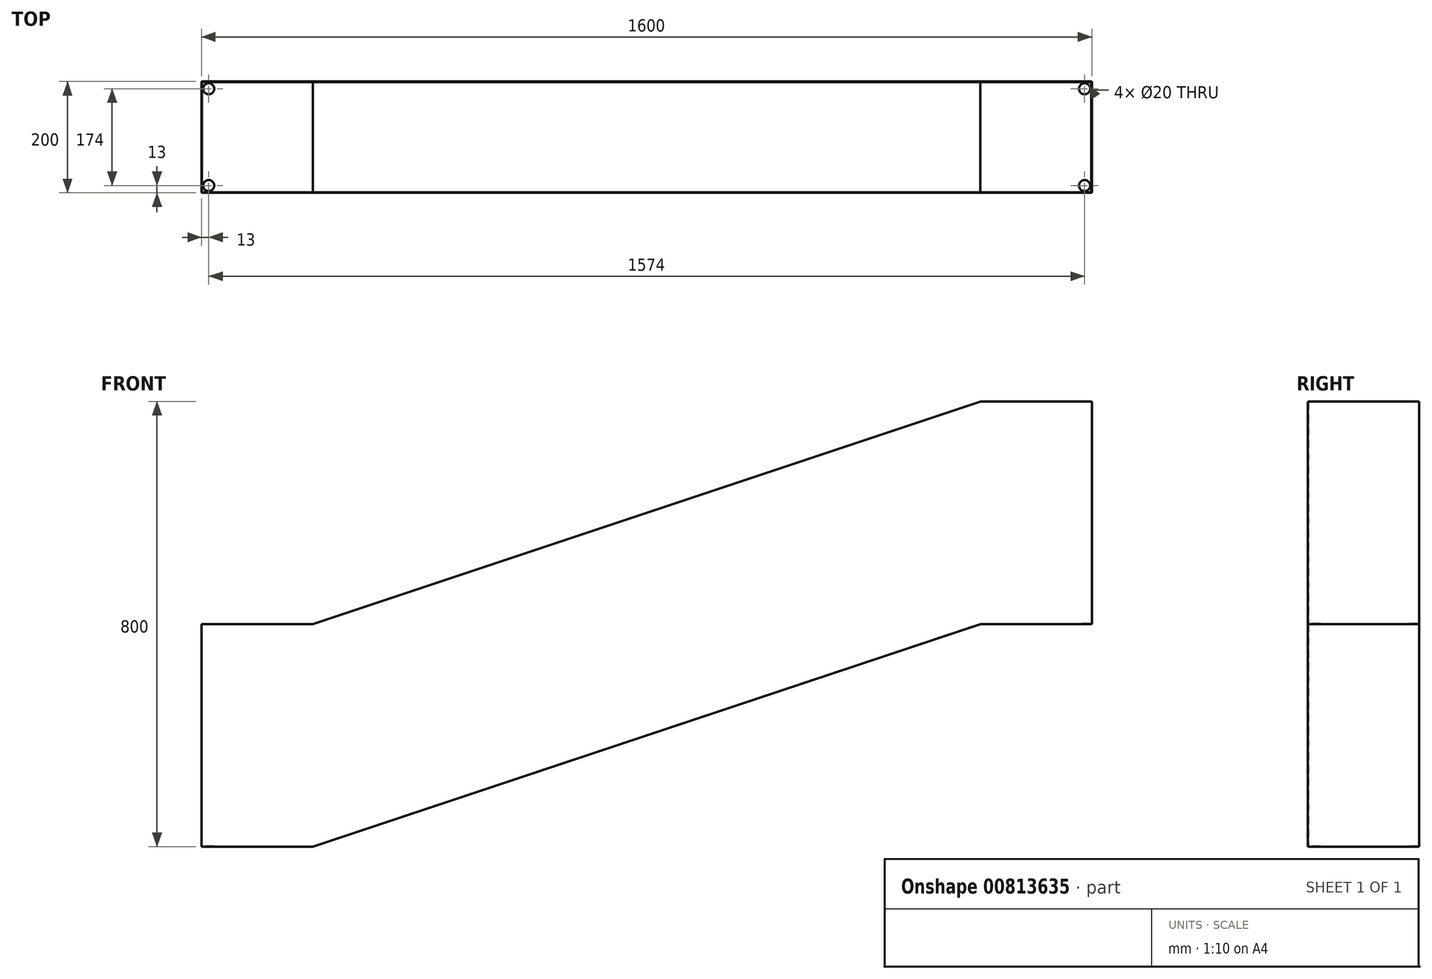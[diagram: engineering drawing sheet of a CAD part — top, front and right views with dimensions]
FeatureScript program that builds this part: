
annotation { "Feature Type Name" : "Feature", "Feature Type Description" : "" }
export const myFeature = defineFeature(function(context is Context, id is Id, definition is map)
    precondition{}
    {
        {
            var Q0;
            Q0=qCreatedBy(makeId("Front.planeOp"),FACE);
            var sketch = newSketch(context, id + "F0", { "sketchPlane" : qUnion([Q0])});
            skLineSegment(sketch, "E0", {"start": v(0, 0) * mm, "end": v(200, 0) * mm});
            skLineSegment(sketch, "E1", {"start": v(200, 0) * mm, "end": v(1400, 400) * mm});
            skLineSegment(sketch, "E2", {"start": v(1400, 400) * mm, "end": v(1600, 400) * mm});
            skLineSegment(sketch, "E3.0", {"start": v(1400, 800) * mm, "end": v(1600, 800) * mm});
            skLineSegment(sketch, "E4.0", {"start": v(0, 400) * mm, "end": v(200, 400) * mm});
            skLineSegment(sketch, "E5", {"start": v(1600, 800) * mm, "end": v(1600, 400) * mm});
            skLineSegment(sketch, "E6", {"start": v(0, 400) * mm, "end": v(0, 0) * mm});
            skLineSegment(sketch, "E7", {"start": v(200, 400) * mm, "end": v(1400, 800) * mm});
            skSolve(sketch);
        }
        {
            var Q0;
            Q0=makeQuery(id+"F0.imprint","IMPRINT",FACE,{"disambiguationData":[TD([[makeQuery(id+"F0.imprint","IMPRINT",EDGE,{"derivedFrom":sQuery(id+"F0.wireOp",EDGE,"E0")}),1.0]])]});
            extrude(context, id + "F1", {"entities" : qUnion([Q0]), "depth" : 200 * mm, "offsetDistance" : 25 * mm});
        }
        {
            var Q0;
            Q0=makeQuery(id+"F1.opExtrude","SWEPT_FACE",FACE,{"disambiguationData":[OSD([sQuery(id+"F0.wireOp",EDGE,"E4.0")])]});
            var Q1;
            Q1=makeQuery(id+"F1.opExtrude","SWEPT_FACE",FACE,{"disambiguationData":[OSD([sQuery(id+"F0.wireOp",EDGE,"E3.0")])]});
            var Q2;
            Q2=makeQuery(id+"F1.opExtrude","SWEPT_FACE",FACE,{"disambiguationData":[OSD([sQuery(id+"F0.wireOp",EDGE,"E7")])]});
            shell(context, id + "F2", {"entities" : qUnion([Q0, Q1, Q2]), "thickness" : 1 * mm});
        }
        {
            var Q0;
            Q0=makeQuery(id+"F2.opShell","OFFSET_FACE",FACE,{"disambiguationData":[OSD([sQuery(id+"F0.wireOp",EDGE,"E2")])]});
            var sketch = newSketch(context, id + "F3", { "sketchPlane" : qUnion([Q0])});
            skCircle(sketch, "E8", {"center": v(1587, -13) * mm, "radius": 12 * mm});
            skCircle(sketch, "E9.0", {"center": v(1587, -13) * mm, "radius": 10 * mm});
            skCircle(sketch, "E10", {"center": v(1587, -187) * mm, "radius": 12 * mm});
            skCircle(sketch, "E11.0", {"center": v(1587, -187) * mm, "radius": 10 * mm});
            skCircle(sketch, "E12", {"center": v(13, -13) * mm, "radius": 12 * mm});
            skCircle(sketch, "E13", {"center": v(13, -187) * mm, "radius": 12 * mm});
            skCircle(sketch, "E14.0", {"center": v(13, -13) * mm, "radius": 10 * mm});
            skCircle(sketch, "E15.0", {"center": v(13, -187) * mm, "radius": 10 * mm});
            skSolve(sketch);
        }
        {
            var Q0;
            Q0=sQuery(id+"F3.wireOp",EDGE,"E9.0");
            var Q1;
            Q1=sQuery(id+"F3.wireOp",EDGE,"E8");
            var Q2;
            Q2=sQuery(id+"F3.wireOp",EDGE,"E11.0");
            var Q3;
            Q3=sQuery(id+"F3.wireOp",EDGE,"E10");
            extrude(context, id + "F4", {"bodyType" : ToolBodyType.SURFACE, "surfaceEntities" : qUnion([Q0, Q1, Q2, Q3]), "depth" : 400 * mm, "offsetDistance" : 25 * mm});
        }
        {
            var Q0;
            Q0=sQuery(id+"F3.wireOp",EDGE,"E14.0");
            var Q1;
            Q1=sQuery(id+"F3.wireOp",EDGE,"E12");
            var Q2;
            Q2=sQuery(id+"F3.wireOp",EDGE,"E15.0");
            var Q3;
            Q3=sQuery(id+"F3.wireOp",EDGE,"E13");
            extrude(context, id + "F5", {"bodyType" : ToolBodyType.SURFACE, "surfaceEntities" : qUnion([Q0, Q1, Q2, Q3]), "oppositeDirection" : true, "depth" : 400 * mm, "offsetDistance" : 25 * mm});
        }
        {
            var Q0;
            Q0=sQuery(id+"F3.wireOp",VERTEX,"E15.0.center");
            var Q1;
            Q1=sQuery(id+"F3.wireOp",VERTEX,"E12.center");
            var Q2;
            Q2=makeQuery(id+"F1.opExtrude","SWEPT_BODY",BODY,{"disambiguationData":[OSD([sQuery(id+"F0.wireOp",EDGE,"E0"),sQuery(id+"F0.wireOp",EDGE,"E1"),sQuery(id+"F0.wireOp",EDGE,"E2"),sQuery(id+"F0.wireOp",EDGE,"E3.0"),sQuery(id+"F0.wireOp",EDGE,"E4.0"),sQuery(id+"F0.wireOp",EDGE,"b94ed2f5-d693-429c-bf34-7d5d2d5847e0"),sQuery(id+"F0.wireOp",EDGE,"E5"),sQuery(id+"F0.wireOp",EDGE,"E6")])]});
            hole(context, id + "F6", {"style" : HoleStyle.SIMPLE, "endStyle" : HoleEndStyle.THROUGH, "holeDiameter" : 20 * mm, "majorDiameter" : 5 * mm, "isTappedThrough" : true, "tappedDepth" : 12 * mm, "tapClearance" : 3, "locations" : qUnion([Q0, Q1]), "scope" : qUnion([Q2])});
        }
        {
            var Q0;
            Q0=sQuery(id+"F3.wireOp",VERTEX,"E8.center");
            var Q1;
            Q1=sQuery(id+"F3.wireOp",VERTEX,"E11.0.center");
            var Q2;
            Q2=makeQuery(id+"F1.opExtrude","SWEPT_BODY",BODY,{"disambiguationData":[OSD([sQuery(id+"F0.wireOp",EDGE,"E0"),sQuery(id+"F0.wireOp",EDGE,"E1"),sQuery(id+"F0.wireOp",EDGE,"E2"),sQuery(id+"F0.wireOp",EDGE,"E3.0"),sQuery(id+"F0.wireOp",EDGE,"E4.0"),sQuery(id+"F0.wireOp",EDGE,"b94ed2f5-d693-429c-bf34-7d5d2d5847e0"),sQuery(id+"F0.wireOp",EDGE,"E5"),sQuery(id+"F0.wireOp",EDGE,"E6")])]});
            hole(context, id + "F7", {"style" : HoleStyle.SIMPLE, "endStyle" : HoleEndStyle.THROUGH, "holeDiameter" : 20 * mm, "majorDiameter" : 5 * mm, "isTappedThrough" : true, "tappedDepth" : 12 * mm, "tapClearance" : 3, "locations" : qUnion([Q0, Q1]), "scope" : qUnion([Q2])});
        }
    });
